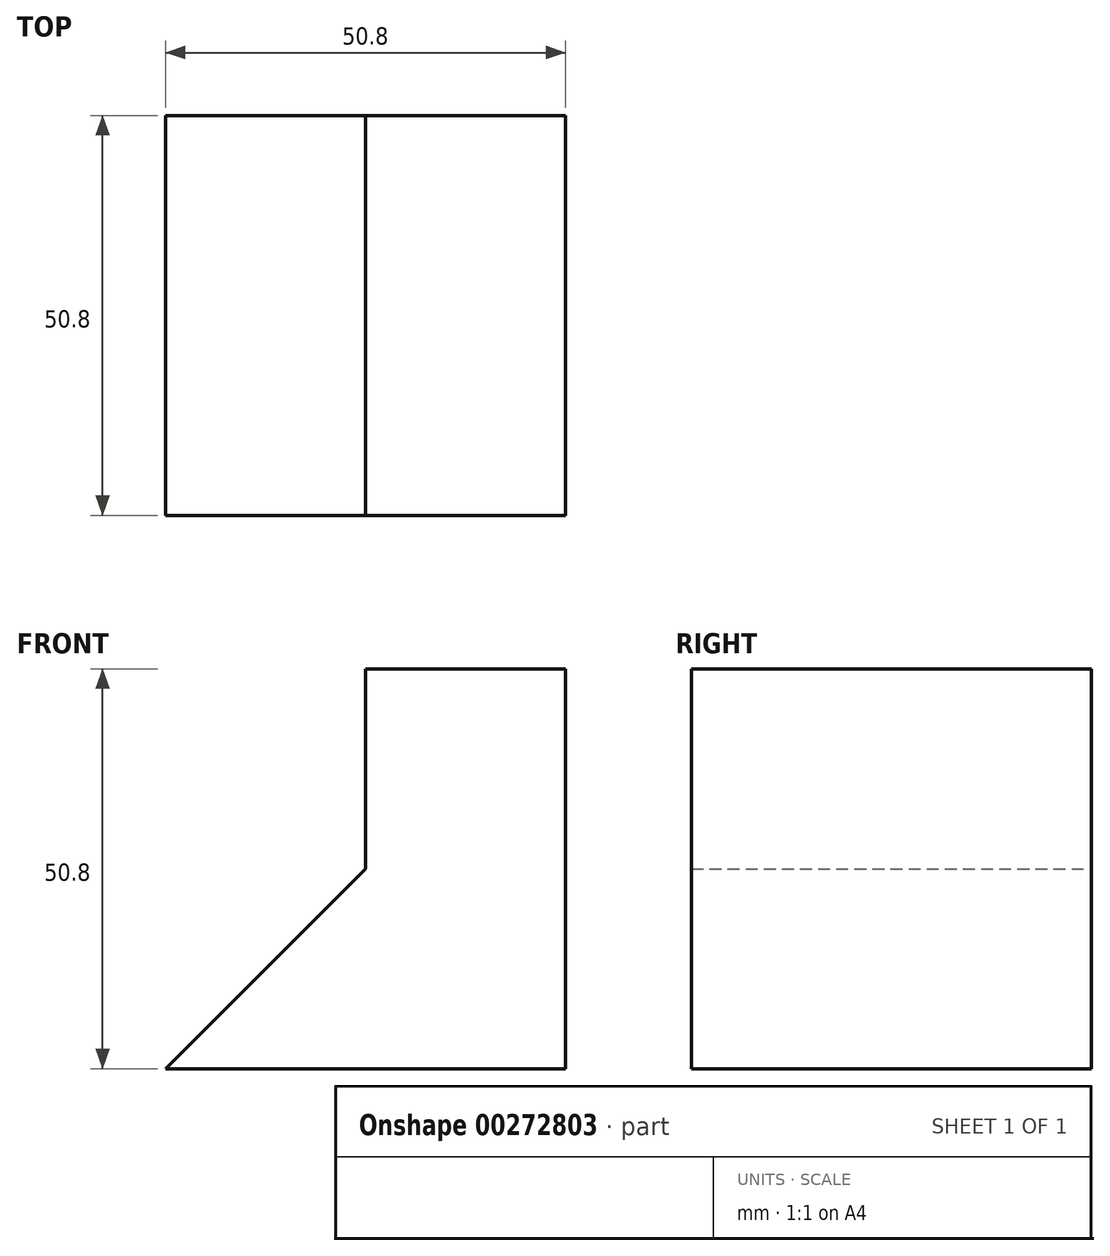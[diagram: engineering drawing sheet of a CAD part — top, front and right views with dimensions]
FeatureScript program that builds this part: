
annotation { "Feature Type Name" : "Feature", "Feature Type Description" : "" }
export const myFeature = defineFeature(function(context is Context, id is Id, definition is map)
    precondition{}
    {
        {
            var Q0;
            Q0=qCreatedBy(makeId("Front.planeOp"),FACE);
            var sketch = newSketch(context, id + "F0", { "sketchPlane" : qUnion([Q0])});
            skLineSegment(sketch, "E0", {"start": v(0, 0) * mm, "end": v(0, 50.8) * mm});
            skLineSegment(sketch, "E1", {"start": v(0, 50.8) * mm, "end": v(-25.4, 50.8) * mm});
            skLineSegment(sketch, "E2", {"start": v(-25.4, 50.8) * mm, "end": v(-25.4, 25.4) * mm});
            skLineSegment(sketch, "E3", {"start": v(0, 0) * mm, "end": v(-50.8, 0) * mm});
            skLineSegment(sketch, "E4", {"start": v(-25.4, 25.4) * mm, "end": v(-50.8, 0) * mm});
            skSolve(sketch);
        }
        {
            var Q0;
            Q0 = qSketchRegion(id + "F0", true);
            extrude(context, id + "F1", {"entities" : qUnion([Q0]), "depth" : 50.8 * mm});
        }
    });
